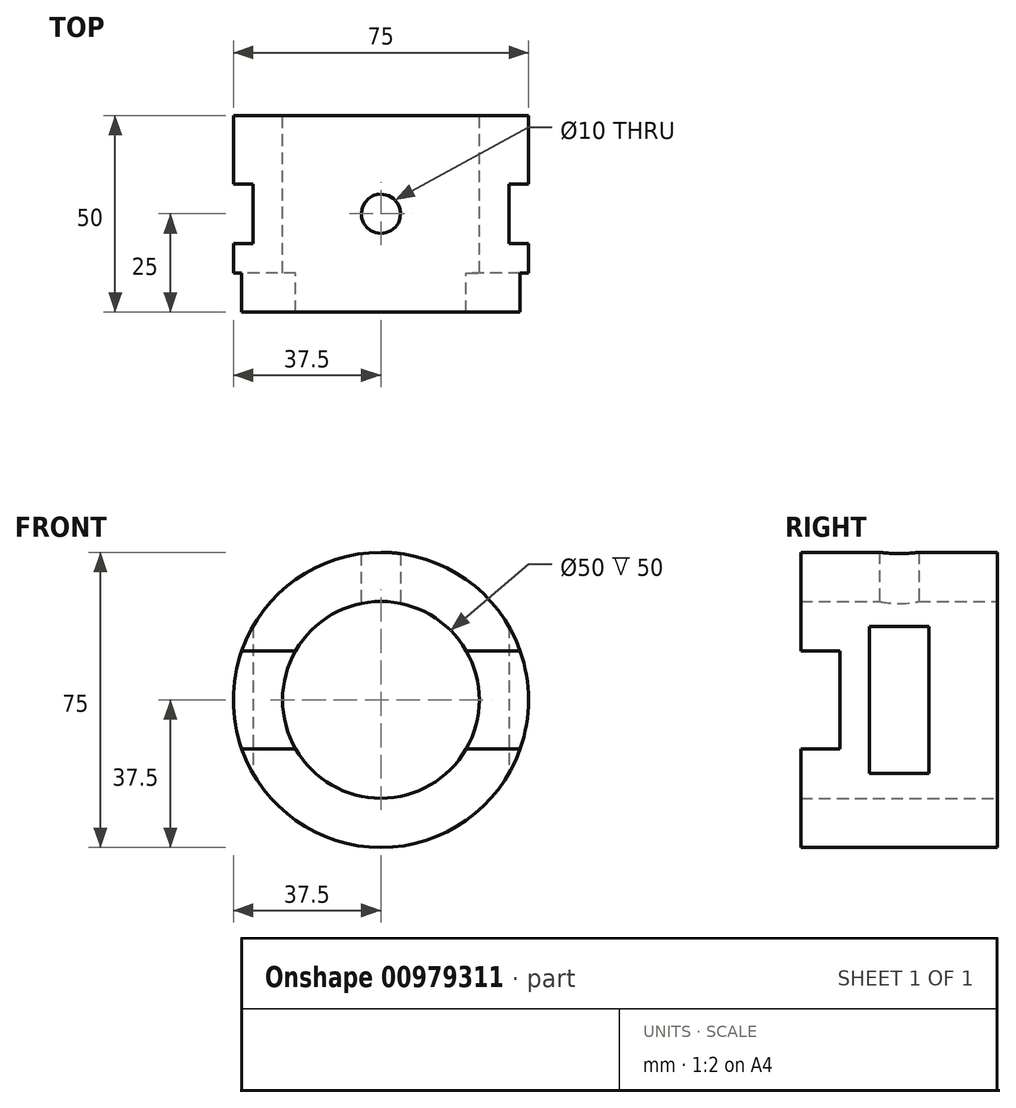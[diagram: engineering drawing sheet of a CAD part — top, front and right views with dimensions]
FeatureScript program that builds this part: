
annotation { "Feature Type Name" : "Feature", "Feature Type Description" : "" }
export const myFeature = defineFeature(function(context is Context, id is Id, definition is map)
    precondition{}
    {
        {
            var Q0;
            Q0=qCreatedBy(makeId("Front.planeOp"),FACE);
            var sketch = newSketch(context, id + "F0", { "sketchPlane" : qUnion([Q0])});
            skCircle(sketch, "E0", {"center": v(0, 0) * mm, "radius": 25 * mm});
            skCircle(sketch, "E1", {"center": v(0, 0) * mm, "radius": 37.5 * mm});
            skSolve(sketch);
        }
        {
            var Q0;
            Q0=makeQuery(id+"F0.imprint","IMPRINT",FACE,{"disambiguationData":[TD([[makeQuery(id+"F0.imprint","IMPRINT",EDGE,{"derivedFrom":sQuery(id+"F0.wireOp",EDGE,"E0")}),-1.0]])]});
            extrude(context, id + "F1", {"entities" : qUnion([Q0]), "endBound" : BoundingType.SYMMETRIC, "depth" : 50 * mm, "offsetDistance" : 25 * mm});
        }
        {
            var Q0;
            Q0=qCreatedBy(makeId("Top.planeOp"),FACE);
            var sketch = newSketch(context, id + "F2", { "sketchPlane" : qUnion([Q0])});
            skCircle(sketch, "E2", {"center": v(0, 0) * mm, "radius": 5 * mm});
            skLineSegment(sketch, "E3", {"start": v(37.5, 25) * mm, "end": v(37.5, -25) * mm});
            skLineSegment(sketch, "E4.bottom", {"start": v(42.5, 7.5) * mm, "end": v(32.5, 7.5) * mm});
            skLineSegment(sketch, "E4.top", {"start": v(42.5, -7.5) * mm, "end": v(32.5, -7.5) * mm});
            skLineSegment(sketch, "E4.left", {"start": v(42.5, 7.5) * mm, "end": v(42.5, -7.5) * mm});
            skLineSegment(sketch, "E4.right", {"start": v(32.5, 7.5) * mm, "end": v(32.5, -7.5) * mm});
            skPoint(sketch, "E4.middle", {"position": v(37.5, 0) * mm});
            skLineSegment(sketch, "E5", {"start": v(0, 32.03) * mm, "end": v(0, -32.83) * mm, "construction": true});
            skLineSegment(sketch, "E6.MirrorCS", {"start": v(-42.5, -7.5) * mm, "end": v(-32.5, -7.5) * mm});
            skLineSegment(sketch, "E7.MirrorCS", {"start": v(-42.5, 7.5) * mm, "end": v(-32.5, 7.5) * mm});
            skLineSegment(sketch, "E8.MirrorCS", {"start": v(-42.5, 7.5) * mm, "end": v(-42.5, -7.5) * mm});
            skPoint(sketch, "E9.MirrorP", {"position": v(-37.5, 0) * mm});
            skLineSegment(sketch, "E10.MirrorCS", {"start": v(-32.5, 7.5) * mm, "end": v(-32.5, -7.5) * mm});
            skLineSegment(sketch, "E11.0", {"start": v(37.5, -25) * mm, "end": v(-37.5, -25) * mm});
            skLineSegment(sketch, "E12", {"start": v(-37.5, -25) * mm, "end": v(-37.5, 25) * mm});
            skLineSegment(sketch, "E13.bottom", {"start": v(37.5, -35) * mm, "end": v(-37.5, -35) * mm});
            skLineSegment(sketch, "E13.top", {"start": v(37.5, -15) * mm, "end": v(-37.5, -15) * mm});
            skLineSegment(sketch, "E13.left", {"start": v(37.5, -35) * mm, "end": v(37.5, -15) * mm});
            skLineSegment(sketch, "E13.right", {"start": v(-37.5, -35) * mm, "end": v(-37.5, -15) * mm});
            skPoint(sketch, "E13.middle", {"position": v(0, -25) * mm});
            skSolve(sketch);
        }
        {
            var Q0;
            Q0=makeQuery(id+"F2.imprint","IMPRINT",FACE,{"disambiguationData":[TD([[makeQuery(id+"F2.imprint","IMPRINT",EDGE,{"derivedFrom":sQuery(id+"F2.wireOp",EDGE,"E2")}),1.0]])]});
            extrude(context, id + "F3", {"entities" : qUnion([Q0]), "operationType" : NewBodyOperationType.REMOVE, "endBound" : BoundingType.THROUGH_ALL, "depth" : 25 * mm, "offsetDistance" : 25 * mm});
        }
        {
            var Q0;
            {var subQ3=sQuery(id+"F2.wireOp",EDGE,"E10.MirrorCS");Q0=makeQuery(id+"F2.imprint","IMPRINT",FACE,{"disambiguationData":[TD([[makeQuery(id+"F2.imprint","IMPRINT",EDGE,{"derivedFrom":subQ3}),-1.0]])]});}
            var Q1;
            {var subQ5=sQuery(id+"F2.wireOp",EDGE,"E4.right");Q1=makeQuery(id+"F2.imprint","IMPRINT",FACE,{"disambiguationData":[TD([[makeQuery(id+"F2.imprint","IMPRINT",EDGE,{"derivedFrom":subQ5}),1.0]])]});}
            extrude(context, id + "F4", {"entities" : qUnion([Q0, Q1]), "operationType" : NewBodyOperationType.REMOVE, "endBound" : BoundingType.SYMMETRIC, "depth" : 75 * mm, "offsetDistance" : 25 * mm});
        }
        {
            var Q0;
            {var subQ2=sQuery(id+"F2.wireOp",EDGE,"E11.0");Q0=makeQuery(id+"F2.imprint","IMPRINT",FACE,{"disambiguationData":[TD([[makeQuery(id+"F2.imprint","IMPRINT",EDGE,{"derivedFrom":subQ2}),-1.0]])]});}
            extrude(context, id + "F5", {"entities" : qUnion([Q0]), "operationType" : NewBodyOperationType.REMOVE, "endBound" : BoundingType.SYMMETRIC, "depth" : 25 * mm, "offsetDistance" : 25 * mm});
        }
    });
